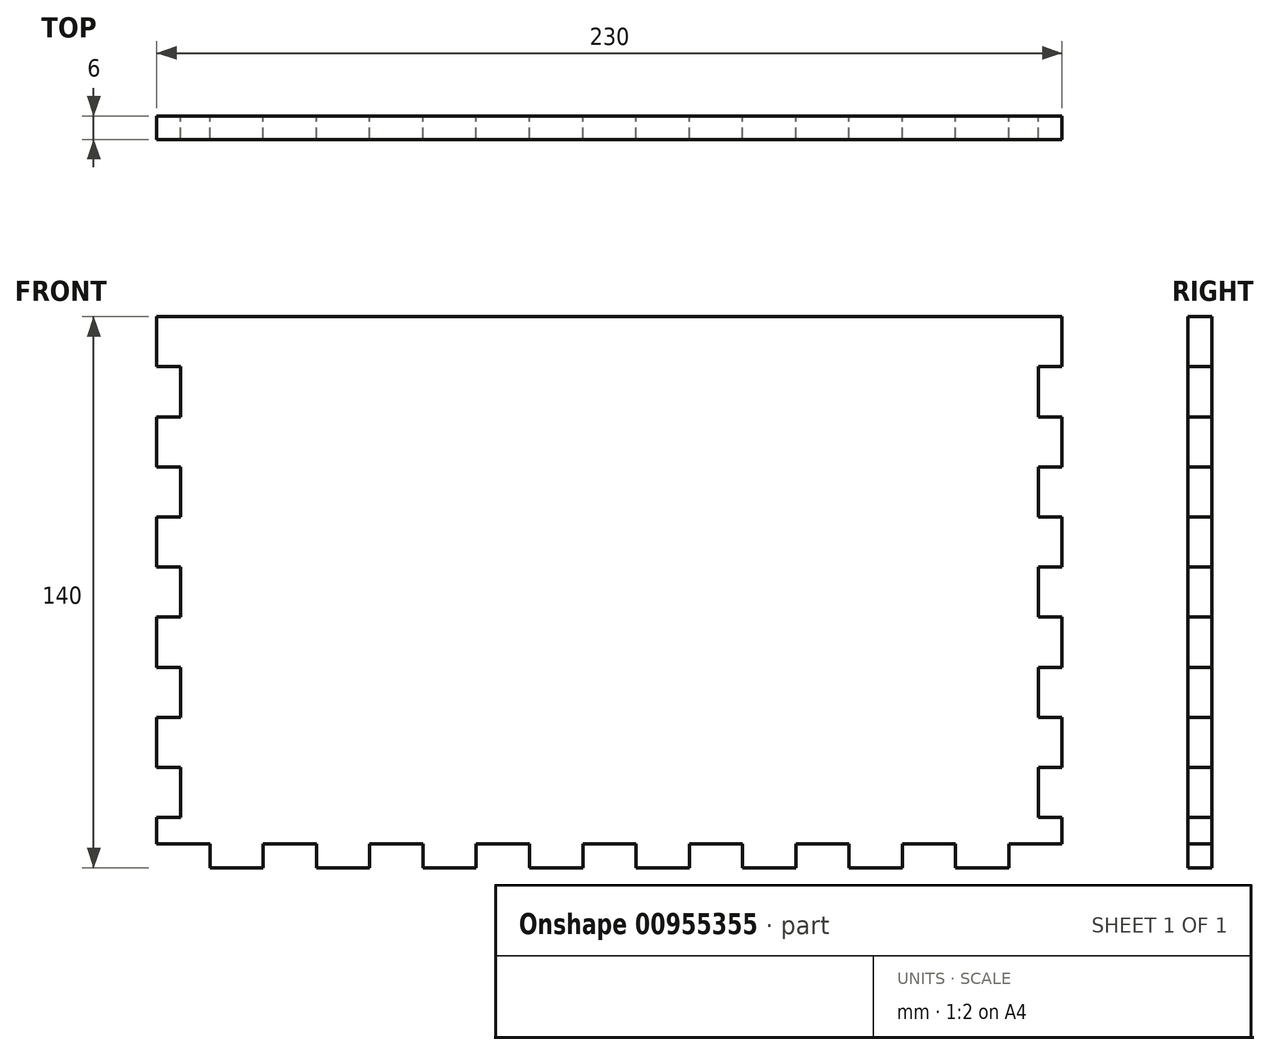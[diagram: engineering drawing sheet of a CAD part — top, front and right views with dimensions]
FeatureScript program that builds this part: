
annotation { "Feature Type Name" : "Feature", "Feature Type Description" : "" }
export const myFeature = defineFeature(function(context is Context, id is Id, definition is map)
    precondition{}
    {
        {
            var Q0;
            Q0=qCreatedBy(makeId("Front.planeOp"),FACE);
            var sketch = newSketch(context, id + "F0", { "sketchPlane" : qUnion([Q0])});
            skLineSegment(sketch, "E0.top", {"start": v(109, 70) * mm, "end": v(-109, 70) * mm});
            skPoint(sketch, "E0.middle", {"position": v(0, 0) * mm});
            skLineSegment(sketch, "E1", {"start": v(-101.47, -70) * mm, "end": v(-101.47, -64) * mm});
            skLineSegment(sketch, "E2", {"start": v(-87.94, -64) * mm, "end": v(-87.94, -70) * mm});
            skLineSegment(sketch, "E3.1.0.0", {"start": v(-60.88, -64) * mm, "end": v(-60.88, -70) * mm});
            skLineSegment(sketch, "E3.1.0.4", {"start": v(-74.41, -70) * mm, "end": v(-74.41, -64) * mm});
            skLineSegment(sketch, "E3.2.0.0", {"start": v(-33.82, -64) * mm, "end": v(-33.82, -70) * mm});
            skLineSegment(sketch, "E3.2.0.4", {"start": v(-47.35, -70) * mm, "end": v(-47.35, -64) * mm});
            skLineSegment(sketch, "E3.3.0.0", {"start": v(-6.76, -64) * mm, "end": v(-6.76, -70) * mm});
            skLineSegment(sketch, "E3.3.0.4", {"start": v(-20.3, -70) * mm, "end": v(-20.3, -64) * mm});
            skLineSegment(sketch, "E3.4.0.0", {"start": v(20.3, -64) * mm, "end": v(20.3, -70) * mm});
            skLineSegment(sketch, "E3.4.0.4", {"start": v(6.76, -70) * mm, "end": v(6.76, -64) * mm});
            skLineSegment(sketch, "E3.5.0.0", {"start": v(47.35, -64) * mm, "end": v(47.35, -70) * mm});
            skLineSegment(sketch, "E3.5.0.4", {"start": v(33.82, -70) * mm, "end": v(33.82, -64) * mm});
            skLineSegment(sketch, "E3.6.0.0", {"start": v(74.41, -64) * mm, "end": v(74.41, -70) * mm});
            skLineSegment(sketch, "E3.6.0.4", {"start": v(60.88, -70) * mm, "end": v(60.88, -64) * mm});
            skLineSegment(sketch, "E3.7.0.0", {"start": v(101.47, -64) * mm, "end": v(101.47, -70) * mm});
            skLineSegment(sketch, "E3.7.0.4", {"start": v(87.94, -70) * mm, "end": v(87.94, -64) * mm});
            skLineSegment(sketch, "E3.direction1", {"start": v(-101.47, -70) * mm, "end": v(-87.94, -70) * mm, "construction": true});
            skLineSegment(sketch, "E4", {"start": v(-115, -64) * mm, "end": v(-115, -57.27) * mm});
            skLineSegment(sketch, "E5", {"start": v(-115, -57.27) * mm, "end": v(-109, -57.27) * mm});
            skLineSegment(sketch, "E6", {"start": v(-109, -57.27) * mm, "end": v(-109, -44.55) * mm});
            skLineSegment(sketch, "E7", {"start": v(-109, -44.55) * mm, "end": v(-115, -44.55) * mm});
            skLineSegment(sketch, "E8", {"start": v(-115, -44.55) * mm, "end": v(-115, -31.82) * mm});
            skLineSegment(sketch, "E9.1.0.0", {"start": v(-109, -31.82) * mm, "end": v(-109, -19.1) * mm});
            skLineSegment(sketch, "E9.1.0.1", {"start": v(-109, -19.1) * mm, "end": v(-115, -19.1) * mm});
            skLineSegment(sketch, "E9.1.0.2", {"start": v(-115, -31.82) * mm, "end": v(-109, -31.82) * mm});
            skLineSegment(sketch, "E9.1.0.3", {"start": v(-115, -19.1) * mm, "end": v(-115, -6.36) * mm});
            skLineSegment(sketch, "E9.2.0.0", {"start": v(-109, -6.36) * mm, "end": v(-109, 6.36) * mm});
            skLineSegment(sketch, "E9.2.0.1", {"start": v(-109, 6.36) * mm, "end": v(-115, 6.36) * mm});
            skLineSegment(sketch, "E9.2.0.2", {"start": v(-115, -6.36) * mm, "end": v(-109, -6.36) * mm});
            skLineSegment(sketch, "E9.2.0.3", {"start": v(-115, 6.36) * mm, "end": v(-115, 19.1) * mm});
            skLineSegment(sketch, "E9.2.0.4", {"start": v(-115, -19.1) * mm, "end": v(-115, -6.36) * mm});
            skLineSegment(sketch, "E9.direction1", {"start": v(-115, -64) * mm, "end": v(-115, -44.55) * mm, "construction": true});
            skLineSegment(sketch, "E10.0.3.0", {"start": v(-109, 19.1) * mm, "end": v(-109, 31.82) * mm});
            skLineSegment(sketch, "E10.3.3.0", {"start": v(-109, 31.82) * mm, "end": v(-115, 31.82) * mm});
            skLineSegment(sketch, "E10.6.3.0", {"start": v(-115, 19.1) * mm, "end": v(-109, 19.1) * mm});
            skLineSegment(sketch, "E10.9.3.0", {"start": v(-115, 31.82) * mm, "end": v(-115, 44.55) * mm});
            skLineSegment(sketch, "E10.0.4.0", {"start": v(-109, 44.55) * mm, "end": v(-109, 57.27) * mm});
            skLineSegment(sketch, "E10.6.4.0", {"start": v(-115, 44.55) * mm, "end": v(-109, 44.55) * mm});
            skLineSegment(sketch, "E10.12.4.0", {"start": v(-115, 31.82) * mm, "end": v(-115, 44.55) * mm});
            skLineSegment(sketch, "E11.MirrorCS", {"start": v(115, 44.55) * mm, "end": v(109, 44.55) * mm});
            skLineSegment(sketch, "E12.MirrorCS", {"start": v(109, -44.55) * mm, "end": v(115, -44.55) * mm});
            skLineSegment(sketch, "E13.MirrorCS", {"start": v(115, -31.82) * mm, "end": v(109, -31.82) * mm});
            skLineSegment(sketch, "E14.MirrorCS", {"start": v(109, -19.1) * mm, "end": v(115, -19.1) * mm});
            skLineSegment(sketch, "E15.MirrorCS", {"start": v(109, 6.36) * mm, "end": v(115, 6.36) * mm});
            skLineSegment(sketch, "E16.MirrorCS", {"start": v(115, -6.36) * mm, "end": v(109, -6.36) * mm});
            skLineSegment(sketch, "E17.MirrorCS", {"start": v(115, -44.55) * mm, "end": v(115, -31.82) * mm});
            skLineSegment(sketch, "E18.MirrorCS", {"start": v(115, -57.27) * mm, "end": v(109, -57.27) * mm});
            skLineSegment(sketch, "E19.MirrorCS", {"start": v(109, 31.82) * mm, "end": v(115, 31.82) * mm});
            skLineSegment(sketch, "E20.MirrorCS", {"start": v(115, 19.1) * mm, "end": v(109, 19.1) * mm});
            skLineSegment(sketch, "E21.MirrorCS", {"start": v(115, 6.36) * mm, "end": v(115, 19.1) * mm});
            skLineSegment(sketch, "E22.MirrorCS", {"start": v(115, 31.82) * mm, "end": v(115, 44.55) * mm});
            skLineSegment(sketch, "E23.MirrorCS", {"start": v(115, -64) * mm, "end": v(115, -57.27) * mm});
            skLineSegment(sketch, "E24.MirrorCS", {"start": v(115, -19.1) * mm, "end": v(115, -6.36) * mm});
            skLineSegment(sketch, "E25.MirrorCS", {"start": v(115, -64) * mm, "end": v(115, -44.55) * mm, "construction": true});
            skLineSegment(sketch, "E26.MirrorCS", {"start": v(109, 19.1) * mm, "end": v(109, 31.82) * mm});
            skLineSegment(sketch, "E27.MirrorCS", {"start": v(109, -6.36) * mm, "end": v(109, 6.36) * mm});
            skLineSegment(sketch, "E28.MirrorCS", {"start": v(109, 44.55) * mm, "end": v(109, 57.27) * mm});
            skLineSegment(sketch, "E29.MirrorCS", {"start": v(109, -57.27) * mm, "end": v(109, -44.55) * mm});
            skLineSegment(sketch, "E30.MirrorCS", {"start": v(109, -31.82) * mm, "end": v(109, -19.1) * mm});
            skLineSegment(sketch, "E31", {"start": v(-115, -64) * mm, "end": v(-101.47, -64) * mm});
            skPoint(sketch, "E31.startSnap0", {"position": v(-115, -63.64) * mm});
            skPoint(sketch, "E31.endSnap0", {"position": v(94.7, -64) * mm});
            skLineSegment(sketch, "E32", {"start": v(101.47, -70) * mm, "end": v(87.94, -70) * mm});
            skPoint(sketch, "E33.orphan", {"position": v(-115, -70) * mm});
            skLineSegment(sketch, "E34.trimOffspring", {"start": v(-87.94, -64) * mm, "end": v(-74.41, -64) * mm});
            skLineSegment(sketch, "E35.trimOffspring", {"start": v(-87.94, -70) * mm, "end": v(-101.47, -70) * mm});
            skLineSegment(sketch, "E36.trimOffspring", {"start": v(-60.88, -64) * mm, "end": v(-47.35, -64) * mm});
            skLineSegment(sketch, "E37.trimOffspring", {"start": v(-60.88, -70) * mm, "end": v(-74.41, -70) * mm});
            skLineSegment(sketch, "E38.trimOffspring", {"start": v(-33.82, -64) * mm, "end": v(-20.3, -64) * mm});
            skLineSegment(sketch, "E39.trimOffspring", {"start": v(-33.82, -70) * mm, "end": v(-47.35, -70) * mm});
            skLineSegment(sketch, "E40.trimOffspring", {"start": v(-6.76, -64) * mm, "end": v(6.76, -64) * mm});
            skLineSegment(sketch, "E41.trimOffspring", {"start": v(-6.76, -70) * mm, "end": v(-20.3, -70) * mm});
            skLineSegment(sketch, "E42.trimOffspring", {"start": v(20.3, -64) * mm, "end": v(33.82, -64) * mm});
            skLineSegment(sketch, "E43.trimOffspring", {"start": v(20.3, -70) * mm, "end": v(6.76, -70) * mm});
            skLineSegment(sketch, "E44.trimOffspring", {"start": v(47.35, -64) * mm, "end": v(60.88, -64) * mm});
            skLineSegment(sketch, "E45.trimOffspring", {"start": v(47.35, -70) * mm, "end": v(33.82, -70) * mm});
            skLineSegment(sketch, "E46.trimOffspring", {"start": v(74.41, -64) * mm, "end": v(87.94, -64) * mm});
            skLineSegment(sketch, "E47.trimOffspring", {"start": v(74.41, -70) * mm, "end": v(60.88, -70) * mm});
            skLineSegment(sketch, "E48.trimOffspring", {"start": v(101.47, -64) * mm, "end": v(115, -64) * mm});
            skPoint(sketch, "E49.orphan", {"position": v(115, 70) * mm});
            skLineSegment(sketch, "E50", {"start": v(-109, 57.27) * mm, "end": v(-115, 57.27) * mm});
            skLineSegment(sketch, "E51", {"start": v(-115, 57.27) * mm, "end": v(-115, 70) * mm});
            skLineSegment(sketch, "E52", {"start": v(-115, 70) * mm, "end": v(-109, 70) * mm});
            skLineSegment(sketch, "E53", {"start": v(109, 57.27) * mm, "end": v(115, 57.27) * mm});
            skLineSegment(sketch, "E54", {"start": v(115, 57.27) * mm, "end": v(115, 70) * mm});
            skLineSegment(sketch, "E55", {"start": v(109, 70) * mm, "end": v(115, 70) * mm});
            skSolve(sketch);
        }
        {
            var Q0;
            Q0=makeQuery(id+"F0.imprint","IMPRINT",FACE,{"disambiguationData":[TD([[makeQuery(id+"F0.imprint","IMPRINT",EDGE,{"derivedFrom":sQuery(id+"F0.wireOp",EDGE,"E0.top")}),1.0]])]});
            extrude(context, id + "F1", {"entities" : qUnion([Q0]), "depth" : 6 * mm, "offsetDistance" : 25 * mm});
        }
    });
